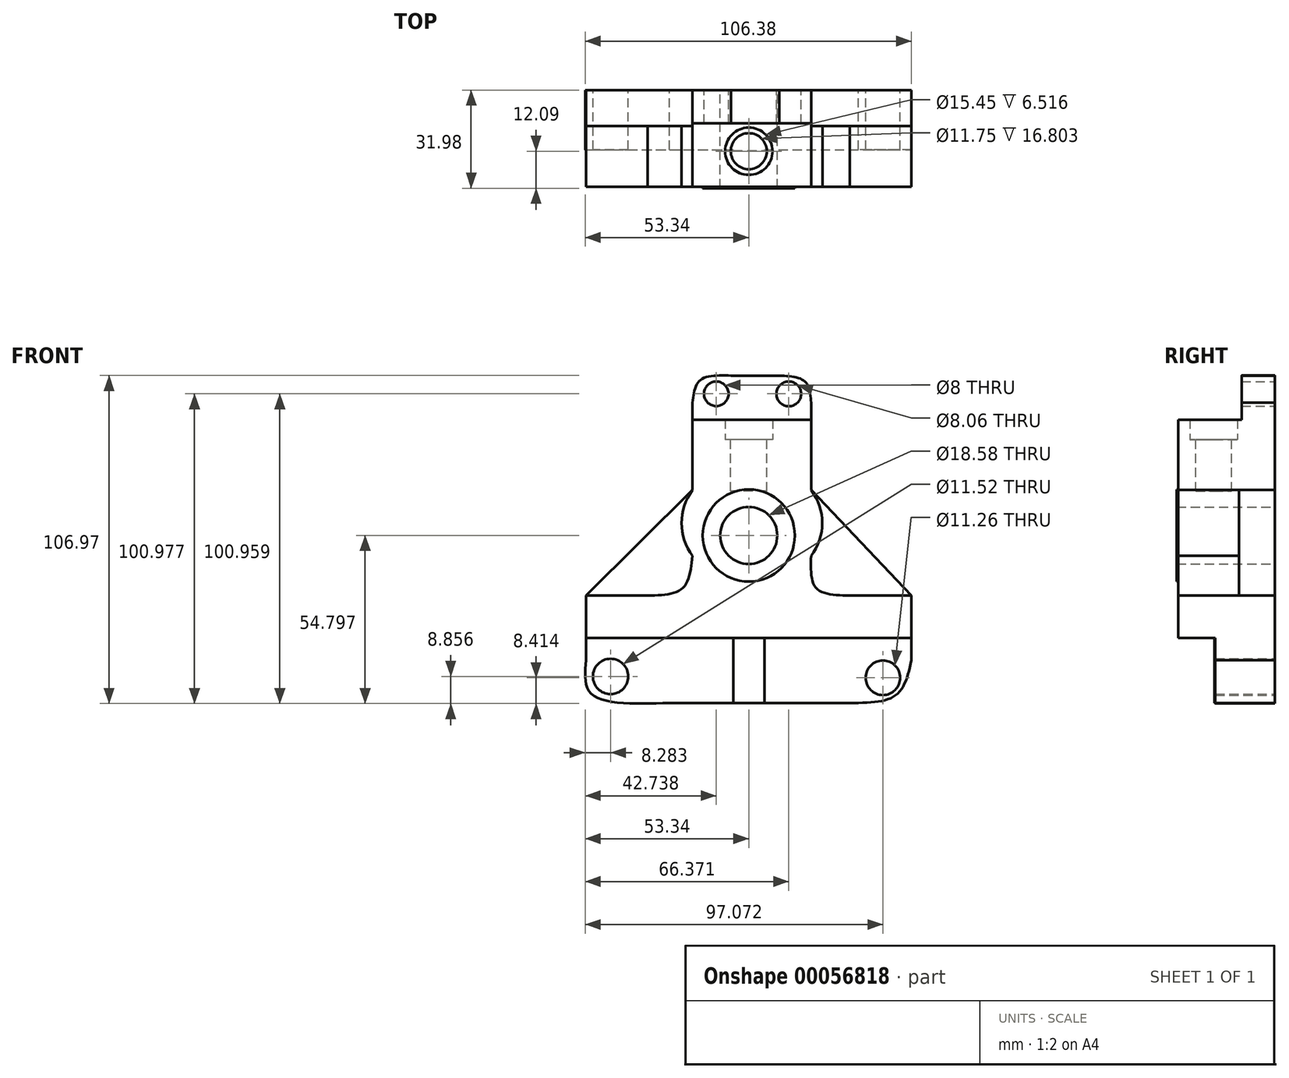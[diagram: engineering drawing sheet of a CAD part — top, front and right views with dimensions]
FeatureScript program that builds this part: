
annotation { "Feature Type Name" : "Feature", "Feature Type Description" : "" }
export const myFeature = defineFeature(function(context is Context, id is Id, definition is map)
    precondition{}
    {
        {
            var Q0;
            Q0=qCreatedBy(makeId("Front.planeOp"),FACE);
            var sketch = newSketch(context, id + "F0", { "sketchPlane" : qUnion([Q0])});
            skLineSegment(sketch, "E0", {"start": v(-53.04, 0) * mm, "end": v(-32.95, 0) * mm});
            skLineSegment(sketch, "E1", {"start": v(53.04, 0) * mm, "end": v(32.95, 0) * mm});
            skFitSpline(sketch, "E2", {"points": [v(32.95, 0) * mm, v(22.09, 2.32) * mm, v(20.32, 12.92) * mm], "startDerivative": vector(-26.07, 0.37) * mm, "endDerivative": vector(0.9, 25.54) * mm});
            skFitSpline(sketch, "E3", {"points": [v(-32.95, 0) * mm, v(-21.65, 2.32) * mm, v(-18.33, 12.92) * mm], "startDerivative": vector(26.35, 0.35) * mm, "endDerivative": vector(2.8, 25.57) * mm});
            skArc(sketch, "E4", {"start": v(-18.33, 34.35) * mm, "mid": v(-21.91, 23.63) * mm, "end": v(-18.33, 12.92) * mm});
            skArc(sketch, "E5", {"start": v(20.32, 12.92) * mm, "mid": v(23.98, 23.63) * mm, "end": v(20.32, 34.35) * mm});
            skLineSegment(sketch, "E6", {"start": v(20.32, 34.35) * mm, "end": v(20.32, 62.84) * mm});
            skLineSegment(sketch, "E7", {"start": v(-18.33, 34.35) * mm, "end": v(-18.33, 62.84) * mm});
            skFitSpline(sketch, "E8", {"points": [v(-18.33, 62.84) * mm, v(-15.9, 70.13) * mm, v(-5.74, 71.67) * mm], "startDerivative": vector(2.06, 18.7) * mm, "endDerivative": vector(22.62, -0.56) * mm});
            skFitSpline(sketch, "E9", {"points": [v(20.32, 62.84) * mm, v(18.33, 69.68) * mm, v(9.94, 71.67) * mm], "startDerivative": vector(-1.35, 16.9) * mm, "endDerivative": vector(-19.13, 1.02) * mm});
            skLineSegment(sketch, "E10", {"start": v(-5.74, 71.67) * mm, "end": v(9.94, 71.67) * mm});
            skCircle(sketch, "E11", {"center": v(-10.6, 65.73) * mm, "radius": 4 * mm});
            skCircle(sketch, "E12", {"center": v(13.03, 65.7) * mm, "radius": 4.03 * mm});
            skLineSegment(sketch, "E13", {"start": v(-18.33, 34.35) * mm, "end": v(-53.04, 0) * mm});
            skLineSegment(sketch, "E14", {"start": v(20.32, 34.35) * mm, "end": v(53.04, 0) * mm});
            skCircle(sketch, "E15", {"center": v(0, 19.55) * mm, "radius": 15.01 * mm});
            skCircle(sketch, "E16", {"center": v(0, 19.55) * mm, "radius": 9.29 * mm});
            skLineSegment(sketch, "E17", {"start": v(-7.15, 32.75) * mm, "end": v(-7.15, 52.24) * mm});
            skLineSegment(sketch, "E18", {"start": v(6.26, 33.2) * mm, "end": v(6.26, 52.24) * mm});
            skLineSegment(sketch, "E19", {"start": v(-18.33, 57.32) * mm, "end": v(20.32, 57.32) * mm});
            skLineSegment(sketch, "E20", {"start": v(-53.04, 0) * mm, "end": v(-53.04, -21.1) * mm});
            skLineSegment(sketch, "E21", {"start": v(53.04, 0) * mm, "end": v(53.04, -21.1) * mm});
            skFitSpline(sketch, "E22", {"points": [v(-53.04, -21.1) * mm, v(-51.24, -32.14) * mm, v(-25.84, -35) * mm], "startDerivative": vector(-2.73, -31.53) * mm, "endDerivative": vector(49.54, 1.69) * mm});
            skFitSpline(sketch, "E23", {"points": [v(53.04, -21.1) * mm, v(48.37, -32.14) * mm, v(35.78, -35) * mm], "startDerivative": vector(-5.64, -27.67) * mm, "endDerivative": vector(-32.78, -0.68) * mm});
            skLineSegment(sketch, "E24", {"start": v(-25.84, -35) * mm, "end": v(35.78, -35) * mm});
            skLineSegment(sketch, "E25", {"start": v(-53.04, -13.83) * mm, "end": v(53.04, -13.83) * mm});
            skCircle(sketch, "E26", {"center": v(-45.06, -26.4) * mm, "radius": 5.76 * mm});
            skCircle(sketch, "E27", {"center": v(43.73, -26.84) * mm, "radius": 5.63 * mm});
            skLineSegment(sketch, "E28", {"start": v(-5.08, -13.83) * mm, "end": v(-5.08, -35) * mm});
            skLineSegment(sketch, "E29", {"start": v(-5.08, -35) * mm, "end": v(5.08, -35) * mm});
            skLineSegment(sketch, "E30", {"start": v(5.08, -35) * mm, "end": v(5.08, -13.83) * mm});
            skSolve(sketch);
        }
        {
            var Q0;
            {var subQ11=sQuery(id+"F0.wireOp",EDGE,"E0");Q0=makeQuery(id+"F0.imprint","IMPRINT",FACE,{"disambiguationData":[TD([[makeQuery(id+"F0.imprint","IMPRINT",EDGE,{"derivedFrom":subQ11}),-1.0]])]});}
            extrude(context, id + "F1", {"entities" : qUnion([Q0]), "depth" : 31.52 * mm});
        }
        {
            var Q0;
            {var subQ1=sQuery(id+"F0.wireOp",EDGE,"E8");Q0=makeQuery(id+"F0.imprint","IMPRINT",FACE,{"disambiguationData":[TD([[makeQuery(id+"F0.imprint","IMPRINT",EDGE,{"derivedFrom":subQ1}),-1.0]])]});}
            extrude(context, id + "F2", {"entities" : qUnion([Q0]), "operationType" : NewBodyOperationType.ADD, "depth" : 10.83 * mm});
        }
        {
            var Q0;
            Q0=makeQuery(id+"F0.imprint","IMPRINT",FACE,{"disambiguationData":[TD([[makeQuery(id+"F0.imprint","IMPRINT",EDGE,{"derivedFrom":sQuery(id+"F0.wireOp",EDGE,"E0")}),1.0]])]});
            var Q1;
            Q1=makeQuery(id+"F0.imprint","IMPRINT",FACE,{"disambiguationData":[TD([[makeQuery(id+"F0.imprint","IMPRINT",EDGE,{"derivedFrom":sQuery(id+"F0.wireOp",EDGE,"E1")}),-1.0]])]});
            extrude(context, id + "F3", {"entities" : qUnion([Q0, Q1]), "operationType" : NewBodyOperationType.ADD, "depth" : 11.67 * mm});
        }
        {
            var Q0;
            Q0=makeQuery(id+"F0.imprint","IMPRINT",FACE,{"disambiguationData":[TD([[makeQuery(id+"F0.imprint","IMPRINT",EDGE,{"derivedFrom":sQuery(id+"F0.wireOp",EDGE,"E16")}),-1.0]])]});
            extrude(context, id + "F4", {"entities" : qUnion([Q0]), "operationType" : NewBodyOperationType.ADD, "depth" : 31.98 * mm});
        }
        {
            var Q0;
            Q0=qCreatedBy(makeId("Top.planeOp"),FACE);
            cPlane(context, id + "F5", {"entities" : qUnion([Q0]), "cplaneType" : CPlaneType.OFFSET, "offset" : 50.8 * mm, "width" : 152.4 * mm, "height" : 152.4 * mm});
        }
        {
            var Q0;
            Q0=qCreatedBy(id+"F5.planeOp",FACE);
            var sketch = newSketch(context, id + "F6", { "sketchPlane" : qUnion([Q0])});
            skCircle(sketch, "E31", {"center": v(0, -19.89) * mm, "radius": 5.87 * mm});
            skCircle(sketch, "E32", {"center": v(0, -19.89) * mm, "radius": 7.73 * mm});
            skSolve(sketch);
        }
        {
            var Q0;
            Q0=makeQuery(id+"F6.imprint","IMPRINT",FACE,{"disambiguationData":[TD([[makeQuery(id+"F6.imprint","IMPRINT",EDGE,{"derivedFrom":sQuery(id+"F6.wireOp",EDGE,"E31")}),-1.0]])]});
            extrude(context, id + "F7", {"entities" : qUnion([Q0]), "operationType" : NewBodyOperationType.REMOVE, "depth" : 7.38 * mm});
        }
        {
            var Q0;
            Q0=sQuery(id+"F6.wireOp",EDGE,"E31");
            extrude(context, id + "F8", {"bodyType" : ToolBodyType.SURFACE, "surfaceEntities" : qUnion([Q0]), "oppositeDirection" : true, "depth" : 8.38 * mm});
        }
        {
            var Q0;
            Q0=makeQuery(id+"F7.boolean.opBoolean","SPLIT",FACE,{"disambiguationData":[TD([makeQuery(id+"F7.opExtrude","SWEPT_FACE",FACE,{"disambiguationData":[OSD([sQuery(id+"F6.wireOp",EDGE,"E31")])]})])],"derivedFrom":makeQuery(id+"F1.opExtrude","SWEPT_FACE",FACE,{"disambiguationData":[OSD([sQuery(id+"F0.wireOp",EDGE,"E19")])]})});
            extrude(context, id + "F9", {"entities" : qUnion([Q0]), "operationType" : NewBodyOperationType.REMOVE, "oppositeDirection" : true, "depth" : 23.32 * mm});
        }
        {
            var Q0;
            {var subQ5=sQuery(id+"F0.wireOp",EDGE,"E22");Q0=makeQuery(id+"F0.imprint","IMPRINT",FACE,{"disambiguationData":[TD([[makeQuery(id+"F0.imprint","IMPRINT",EDGE,{"derivedFrom":subQ5}),1.0]])]});}
            var Q1;
            {var subQ5=sQuery(id+"F0.wireOp",EDGE,"E23");Q1=makeQuery(id+"F0.imprint","IMPRINT",FACE,{"disambiguationData":[TD([[makeQuery(id+"F0.imprint","IMPRINT",EDGE,{"derivedFrom":subQ5}),-1.0]])]});}
            var Q2;
            {var subQ0=sQuery(id+"F0.wireOp",EDGE,"cBYG7uF3-yb7C-LOaZ-kWaM-1tIK2xPpJ0VH");var subQ1=sQuery(id+"F0.wireOp",EDGE,"E24");var subQ2=makeQuery(id+"F0.imprint","INTERSECT",VERTEX,{"derivedFrom":[subQ1,subQ0]});Q2=makeQuery(id+"F0.imprint","IMPRINT",FACE,{"disambiguationData":[TD([[makeQuery(id+"F0.imprint","IMPRINT",EDGE,{"disambiguationData":[TD([[subQ2,-1.0]])],"derivedFrom":subQ1}),1.0]])]});}
            var Q3;
            {var subQ5=sQuery(id+"F0.wireOp",EDGE,"Mmimg2d5-xP4X-IgNx-SFCl-YxnJDaBdTWgU");Q3=makeQuery(id+"F0.imprint","IMPRINT",FACE,{"disambiguationData":[TD([[makeQuery(id+"F0.imprint","IMPRINT",EDGE,{"derivedFrom":subQ5}),1.0]])]});}
            extrude(context, id + "F10", {"entities" : qUnion([Q0, Q1, Q2, Q3]), "operationType" : NewBodyOperationType.ADD, "depth" : 19.41 * mm});
        }
        {
            var Q0;
            {var subQ0=sQuery(id+"F0.wireOp",EDGE,"E28");Q0=makeQuery(id+"F0.imprint","IMPRINT",FACE,{"disambiguationData":[TD([[makeQuery(id+"F0.imprint","IMPRINT",EDGE,{"derivedFrom":subQ0}),1.0]])]});}
            extrude(context, id + "F11", {"entities" : qUnion([Q0]), "operationType" : NewBodyOperationType.ADD, "depth" : 19.66 * mm});
        }
    });
